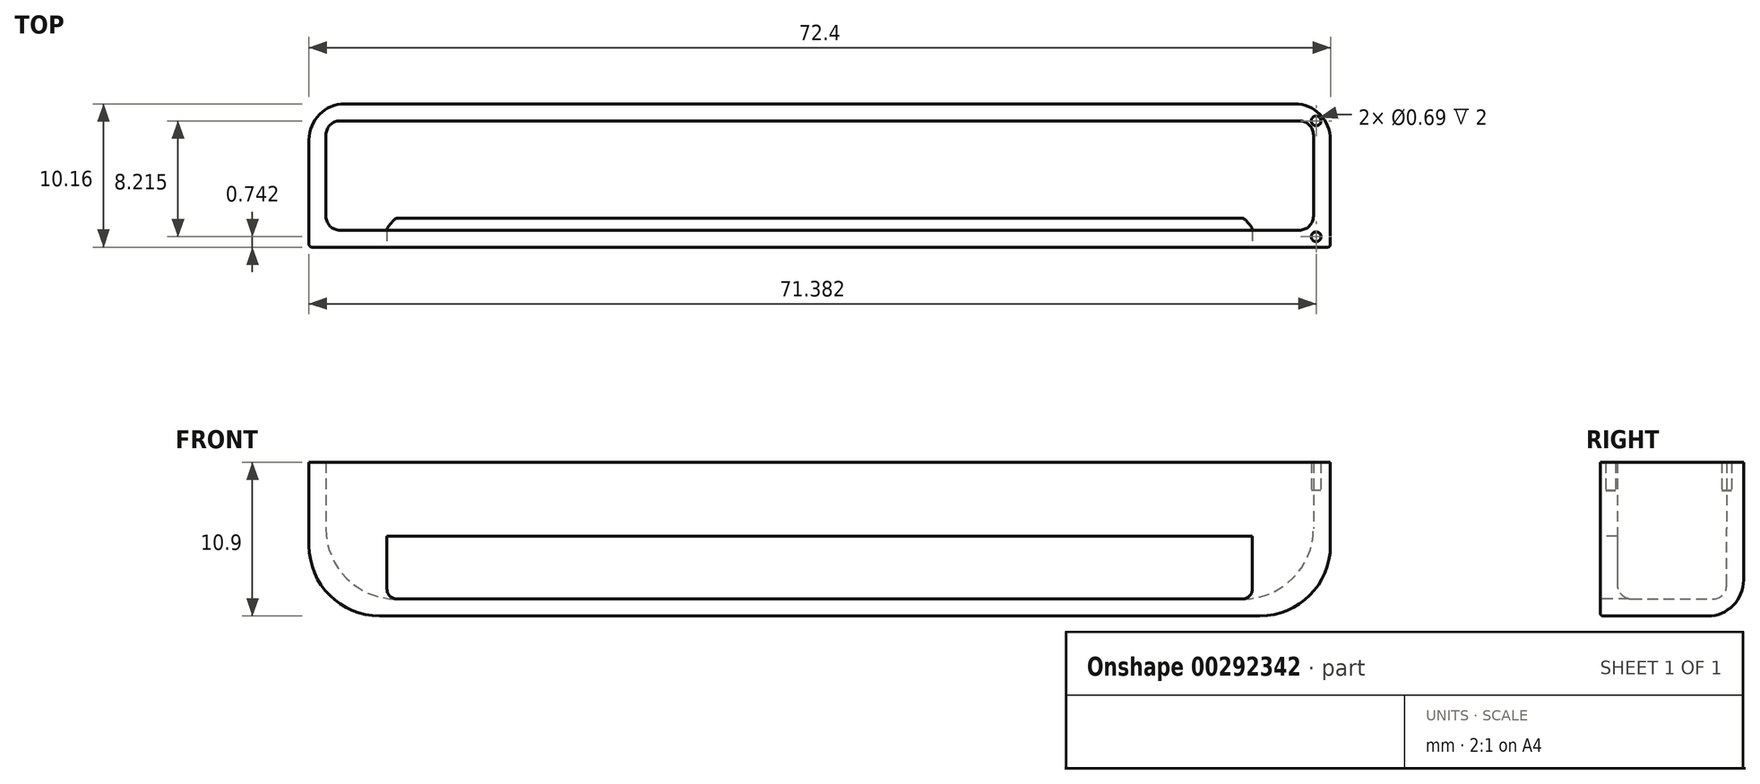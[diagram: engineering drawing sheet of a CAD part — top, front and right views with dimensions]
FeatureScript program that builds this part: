
annotation { "Feature Type Name" : "Feature", "Feature Type Description" : "" }
export const myFeature = defineFeature(function(context is Context, id is Id, definition is map)
    precondition{}
    {
        {
            var Q0;
            Q0=qCreatedBy(makeId("Front.planeOp"),FACE);
            var sketch = newSketch(context, id + "F0", { "sketchPlane" : qUnion([Q0])});
            skLineSegment(sketch, "E0.bottom", {"start": v(36.2, 4.45) * mm, "end": v(-36.2, 4.45) * mm});
            skLineSegment(sketch, "E0.top", {"start": v(36.2, -4.44) * mm, "end": v(-36.2, -4.44) * mm});
            skLineSegment(sketch, "E0.left", {"start": v(36.2, 4.45) * mm, "end": v(36.2, -4.44) * mm});
            skLineSegment(sketch, "E0.right", {"start": v(-36.2, 4.45) * mm, "end": v(-36.2, -4.44) * mm});
            skPoint(sketch, "E0.middle", {"position": v(0, 0) * mm});
            skSolve(sketch);
        }
        {
            var Q0;
            Q0=makeQuery(id+"F0.imprint","IMPRINT",FACE,{"disambiguationData":[TD([[makeQuery(id+"F0.imprint","IMPRINT",EDGE,{"derivedFrom":sQuery(id+"F0.wireOp",EDGE,"E0.bottom")}),1.0]])]});
            extrude(context, id + "F1", {"entities" : qUnion([Q0]), "depth" : 10.16 * mm});
        }
        {
            var Q0;
            Q0=makeQuery(id+"F1.opExtrude","SWEPT_FACE",FACE,{"disambiguationData":[OSD([sQuery(id+"F0.wireOp",EDGE,"E0.bottom")])]});
            shell(context, id + "F2", {"entities" : qUnion([Q0]), "thickness" : 1.2 * mm});
        }
        {
            var Q0;
            Q0=makeQuery(id+"F1.opExtrude","SWEPT_EDGE",EDGE,{"disambiguationData":[OSD([sQuery(id+"F0.wireOp",EDGE,"E0.top"),sQuery(id+"F0.wireOp",EDGE,"E0.right")])]});
            var Q1;
            Q1=makeQuery(id+"F1.opExtrude","SWEPT_EDGE",EDGE,{"disambiguationData":[OSD([sQuery(id+"F0.wireOp",EDGE,"E0.top"),sQuery(id+"F0.wireOp",EDGE,"E0.left")])]});
            var Q2;
            Q2=makeQuery(id+"F2.opShell","OFFSET_EDGE",EDGE,{"disambiguationData":[OSD([sQuery(id+"F0.wireOp",EDGE,"E0.top"),sQuery(id+"F0.wireOp",EDGE,"E0.right")])]});
            var Q3;
            Q3=makeQuery(id+"F2.opShell","OFFSET_EDGE",EDGE,{"disambiguationData":[OSD([sQuery(id+"F0.wireOp",EDGE,"E0.top"),sQuery(id+"F0.wireOp",EDGE,"E0.left")])]});
            fillet(context, id + "F3", {"entities" : qUnion([Q0, Q1, Q2, Q3]), "radius" : 5 * mm, "tangentPropagation" : true, "allowEdgeOverflow" : false});
        }
        {
            var Q0;
            Q0=makeQuery(id+"F1.opExtrude","CAP_EDGE",EDGE,{"disambiguationData":[OSD([sQuery(id+"F0.wireOp",EDGE,"E0.top")])],"isStart":true});
            fillet(context, id + "F4", {"entities" : qUnion([Q0]), "radius" : 2.54 * mm, "tangentPropagation" : true, "allowEdgeOverflow" : false});
        }
        {
            var Q0;
            Q0=makeQuery(id+"F1.opExtrude","CAP_EDGE",EDGE,{"disambiguationData":[OSD([sQuery(id+"F0.wireOp",EDGE,"E0.top")])],"isStart":false});
            fillet(context, id + "F5", {"entities" : qUnion([Q0]), "radius" : 0.2 * mm, "tangentPropagation" : true, "allowEdgeOverflow" : false});
        }
        {
            var Q0;
            Q0=makeQuery(id+"F1.opExtrude","CAP_FACE",FACE,{"disambiguationData":[OSD([sQuery(id+"F0.wireOp",EDGE,"E0.bottom"),sQuery(id+"F0.wireOp",EDGE,"E0.top"),sQuery(id+"F0.wireOp",EDGE,"E0.left"),sQuery(id+"F0.wireOp",EDGE,"E0.right")])],"isStart":false});
            var sketch = newSketch(context, id + "F6", { "sketchPlane" : qUnion([Q0])});
            skLineSegment(sketch, "E1.bottom", {"start": v(30.67, 1.2) * mm, "end": v(-30.67, 1.2) * mm});
            skLineSegment(sketch, "E1.top", {"start": v(30.67, -3.23) * mm, "end": v(-30.67, -3.23) * mm});
            skLineSegment(sketch, "E1.left", {"start": v(30.67, 1.2) * mm, "end": v(30.67, -3.23) * mm});
            skLineSegment(sketch, "E1.right", {"start": v(-30.67, 1.2) * mm, "end": v(-30.67, -3.23) * mm});
            skPoint(sketch, "E1.middle", {"position": v(0, -1.02) * mm});
            skSolve(sketch);
        }
        {
            var Q0;
            Q0=makeQuery(id+"F6.imprint","IMPRINT",FACE,{"disambiguationData":[TD([[makeQuery(id+"F6.imprint","IMPRINT",EDGE,{"derivedFrom":sQuery(id+"F6.wireOp",EDGE,"E1.bottom")}),1.0]])]});
            extrude(context, id + "F7", {"entities" : qUnion([Q0]), "operationType" : NewBodyOperationType.REMOVE, "oppositeDirection" : true, "depth" : 2 * mm});
        }
        {
            var Q0;
            Q0=makeQuery(id+"F7.boolean.opBoolean","COPY",EDGE,{"derivedFrom":makeQuery(id+"F7.opExtrude","SWEPT_EDGE",EDGE,{"disambiguationData":[OSD([sQuery(id+"F6.wireOp",EDGE,"E1.top"),sQuery(id+"F6.wireOp",EDGE,"E1.left")])]})});
            var Q1;
            Q1=makeQuery(id+"F7.boolean.opBoolean","COPY",EDGE,{"derivedFrom":makeQuery(id+"F7.opExtrude","SWEPT_EDGE",EDGE,{"disambiguationData":[OSD([sQuery(id+"F6.wireOp",EDGE,"E1.top"),sQuery(id+"F6.wireOp",EDGE,"E1.right")])]})});
            fillet(context, id + "F8", {"entities" : qUnion([Q0, Q1]), "radius" : .7 * mm, "tangentPropagation" : true, "allowEdgeOverflow" : false});
        }
        {
            var Q0;
            {var subQ0=sQuery(id+"F0.wireOp",EDGE,"E0.right");Q0=makeQuery(id+"F2.opShell","OFFSET_EDGE",EDGE,{"disambiguationData":[OSD([subQ0]),TDD([makeQuery(id+"F1.opExtrude","CAP_EDGE",EDGE,{"disambiguationData":[OSD([subQ0])],"isStart":true})])]});}
            var Q1;
            {var subQ0=sQuery(id+"F0.wireOp",EDGE,"E0.right");var subQ1=sQuery(id+"F0.wireOp",EDGE,"E0.left");var subQ2=sQuery(id+"F0.wireOp",EDGE,"E0.top");var subQ3=sQuery(id+"F0.wireOp",EDGE,"E0.bottom");var subQ4=makeQuery(id+"F2.opShell","OFFSET_FACE",FACE,{"disambiguationData":[OSD([subQ3,subQ2,subQ1,subQ0]),TDD([makeQuery(id+"F1.opExtrude","CAP_FACE",FACE,{"disambiguationData":[OSD([subQ3,subQ2,subQ1,subQ0])],"isStart":false})])]});var subQ5=makeQuery(id+"F2.opShell","OFFSET_EDGE",EDGE,{"disambiguationData":[OSD([subQ2,subQ1])]});var subQ7=makeQuery(id+"F3.opFillet","BLEND_EDGE",EDGE,{"blendedFrom":[subQ5,subQ4],"blendedInto":[subQ4]});Q1=makeQuery(id+"F8.opFillet","MERGE",EDGE,{"derivedFrom":[makeQuery(id+"F7.boolean.opBoolean","SPLIT",EDGE,{"disambiguationData":[TD([makeQuery(id+"F2.opShell","OFFSET_FACE",FACE,{"disambiguationData":[OSD([subQ2])]})])],"derivedFrom":subQ7}),makeQuery(id+"F7.boolean.opBoolean","SPLIT",EDGE,{"disambiguationData":[TD([makeQuery(id+"F2.opShell","OFFSET_FACE",FACE,{"disambiguationData":[OSD([subQ1])]})])],"derivedFrom":subQ7})]});}
            fillet(context, id + "F9", {"entities" : qUnion([Q0, Q1]), "radius" : 1 * mm, "tangentPropagation" : true, "allowEdgeOverflow" : false});
        }
        {
            var Q0;
            Q0=makeQuery(id+"F1.opExtrude","SWEPT_FACE",FACE,{"disambiguationData":[OSD([sQuery(id+"F0.wireOp",EDGE,"E0.bottom")])]});
            var sketch = newSketch(context, id + "F10", { "sketchPlane" : qUnion([Q0])});
            skCircle(sketch, "E2", {"center": v(-35.18, -1.2) * mm, "radius": 0.35 * mm});
            skCircle(sketch, "E3.MirrorC", {"center": v(35.18, -1.2) * mm, "radius": 0.35 * mm});
            skCircle(sketch, "E4", {"center": v(-35.18, -9.42) * mm, "radius": 0.35 * mm});
            skCircle(sketch, "E5.MirrorC", {"center": v(35.18, -9.42) * mm, "radius": 0.35 * mm});
            skSolve(sketch);
        }
        {
            var Q0;
            Q0=makeQuery(id+"F10.imprint","IMPRINT",FACE,{"disambiguationData":[TD([[makeQuery(id+"F10.imprint","IMPRINT",EDGE,{"derivedFrom":sQuery(id+"F10.wireOp",EDGE,"E2")}),1.0]])]});
            var Q1;
            Q1=makeQuery(id+"F10.imprint","IMPRINT",FACE,{"disambiguationData":[TD([[makeQuery(id+"F10.imprint","IMPRINT",EDGE,{"derivedFrom":sQuery(id+"F10.wireOp",EDGE,"E4")}),1.0]])]});
            var Q2;
            Q2=makeQuery(id+"F10.imprint","IMPRINT",FACE,{"disambiguationData":[TD([[makeQuery(id+"F10.imprint","IMPRINT",EDGE,{"derivedFrom":sQuery(id+"F10.wireOp",EDGE,"E3.MirrorC")}),-1.0]])]});
            var Q3;
            Q3=makeQuery(id+"F10.imprint","IMPRINT",FACE,{"disambiguationData":[TD([[makeQuery(id+"F10.imprint","IMPRINT",EDGE,{"derivedFrom":sQuery(id+"F10.wireOp",EDGE,"E5.MirrorC")}),-1.0]])]});
            extrude(context, id + "F11", {"entities" : qUnion([Q0, Q1, Q2, Q3]), "operationType" : NewBodyOperationType.ADD, "depth" : 2 * mm});
        }
    });
